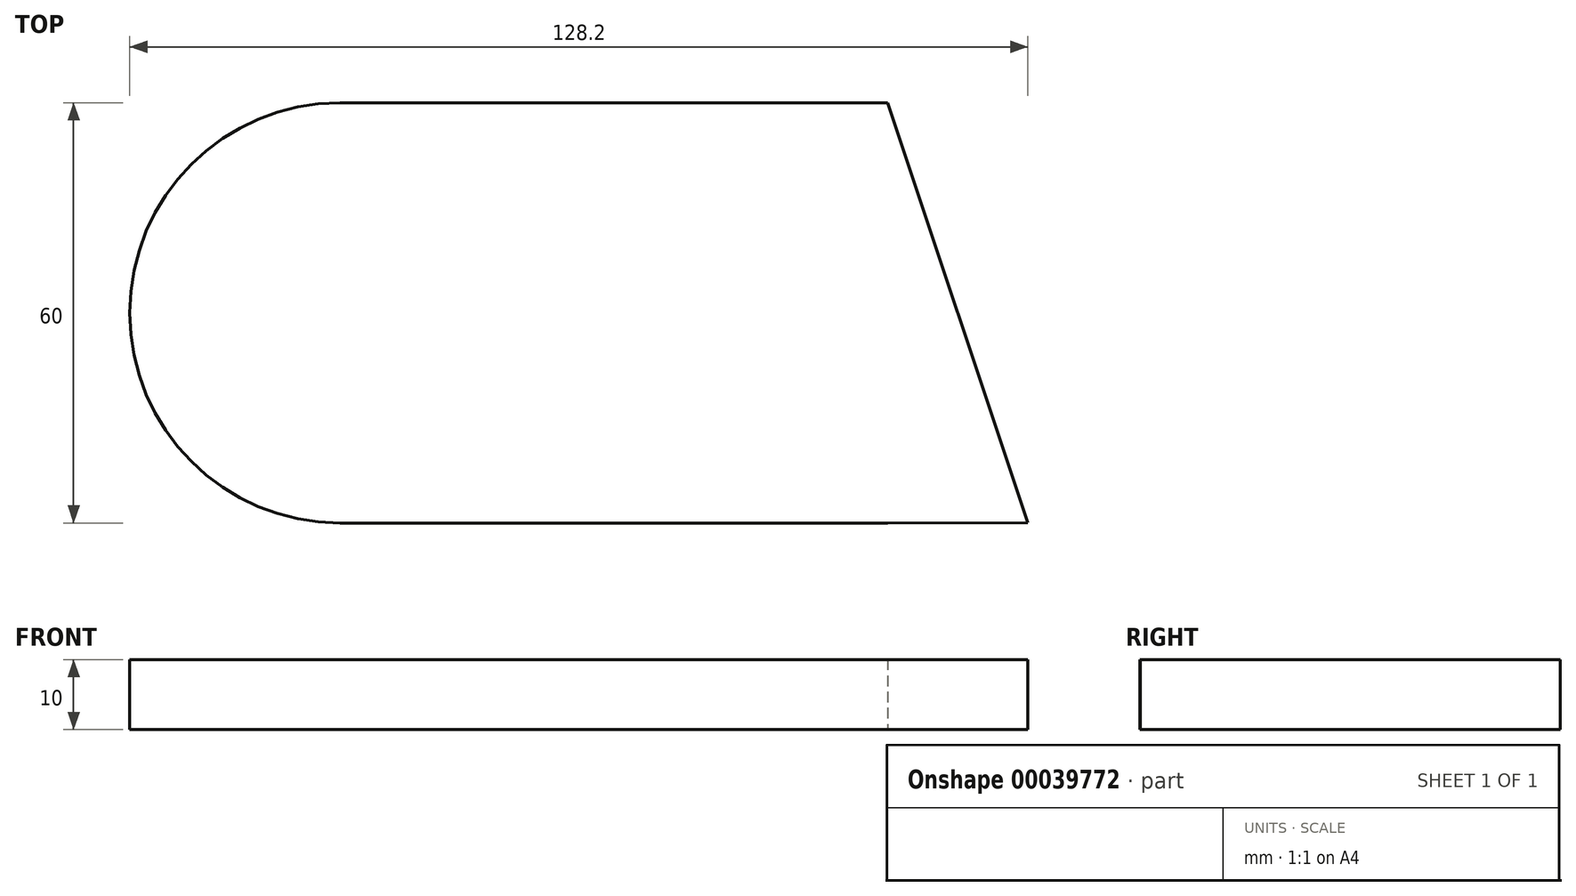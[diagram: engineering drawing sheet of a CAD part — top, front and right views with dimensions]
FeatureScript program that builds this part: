
annotation { "Feature Type Name" : "Feature", "Feature Type Description" : "" }
export const myFeature = defineFeature(function(context is Context, id is Id, definition is map)
    precondition{}
    {
        {
            var Q0;
            Q0=qCreatedBy(makeId("Top.planeOp"),FACE);
            var sketch = newSketch(context, id + "F0", { "sketchPlane" : qUnion([Q0])});
            skLineSegment(sketch, "E0.rect.bottom", {"start": v(-39.1, 30) * mm, "end": v(39.1, 30) * mm});
            skLineSegment(sketch, "E0.rect.top", {"start": v(-39.1, -30) * mm, "end": v(39.1, -30) * mm});
            skLineSegment(sketch, "E0.rect.left", {"start": v(-39.1, 30) * mm, "end": v(-39.1, -30) * mm});
            skLineSegment(sketch, "E0.rect.right", {"start": v(39.1, 30) * mm, "end": v(39.1, -30) * mm});
            skPoint(sketch, "E0.rect.middle", {"position": v(0, 0) * mm});
            skLineSegment(sketch, "E1", {"start": v(39.1, 30) * mm, "end": v(59.1, -29.95) * mm});
            skLineSegment(sketch, "E2", {"start": v(59.1, -29.95) * mm, "end": v(39.1, -30) * mm});
            skArc(sketch, "E3", {"start": v(-39.1, 30) * mm, "mid": v(-69.1, 0) * mm, "end": v(-39.1, -30) * mm});
            skPoint(sketch, "E3.third.point", {"position": v(-69.1, 0) * mm});
            skSolve(sketch);
        }
        {
            var Q0;
            Q0=makeQuery(id+"F0.imprint","IMPRINT",FACE,{"disambiguationData":[TD([[makeQuery(id+"F0.imprint","IMPRINT",EDGE,{"derivedFrom":sQuery(id+"F0.wireOp",EDGE,"E0.rect.right")}),1.0]])]});
            var Q1;
            Q1=makeQuery(id+"F0.imprint","IMPRINT",FACE,{"disambiguationData":[TD([[makeQuery(id+"F0.imprint","IMPRINT",EDGE,{"derivedFrom":sQuery(id+"F0.wireOp",EDGE,"E0.rect.bottom")}),-1.0]])]});
            var Q2;
            Q2=makeQuery(id+"F0.imprint","IMPRINT",FACE,{"disambiguationData":[TD([[makeQuery(id+"F0.imprint","IMPRINT",EDGE,{"derivedFrom":sQuery(id+"F0.wireOp",EDGE,"E0.rect.left")}),-1.0]])]});
            extrude(context, id + "F1", {"entities" : qUnion([Q0, Q1, Q2]), "depth" : 10 * mm});
        }
    });
